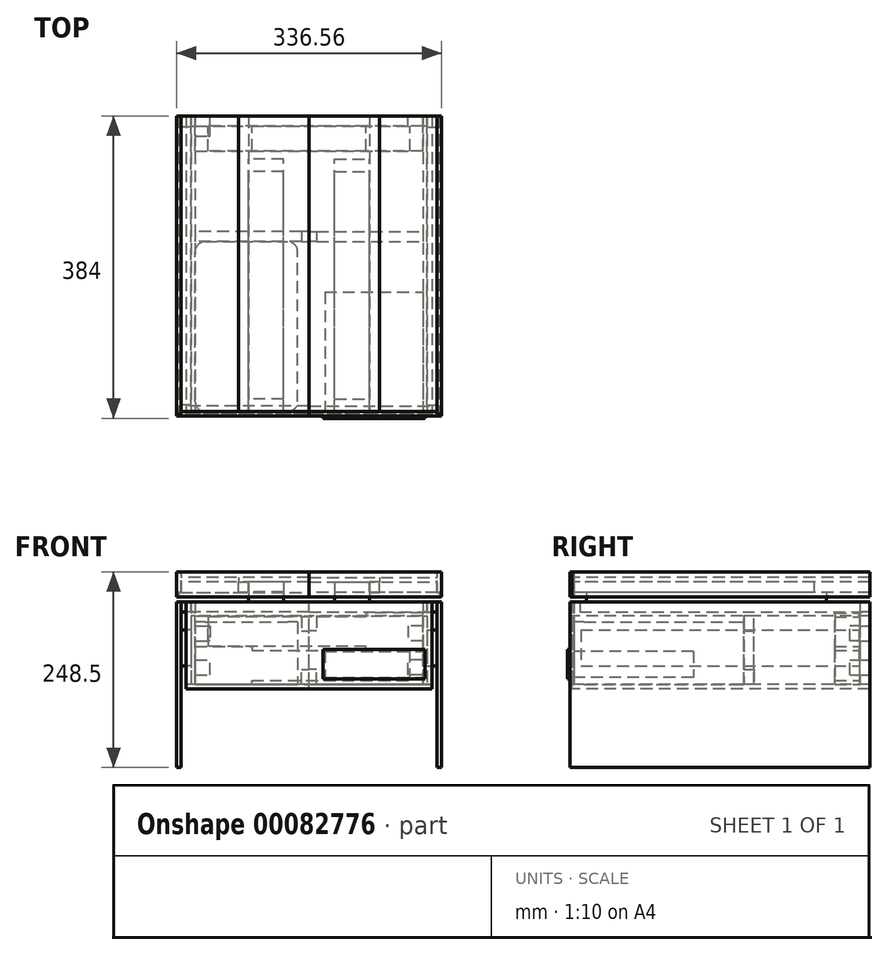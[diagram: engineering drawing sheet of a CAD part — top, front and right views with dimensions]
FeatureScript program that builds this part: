
annotation { "Feature Type Name" : "Feature", "Feature Type Description" : "" }
export const myFeature = defineFeature(function(context is Context, id is Id, definition is map)
    precondition{}
    {
        {
            var Q0;
            Q0=qCreatedBy(makeId("Front.planeOp"),FACE);
            var sketch = newSketch(context, id + "F0", { "sketchPlane" : qUnion([Q0])});
            skLineSegment(sketch, "E0.bottom", {"start": v(-168.28, 0) * mm, "end": v(-162.78, 0) * mm});
            skLineSegment(sketch, "E0.top", {"start": v(-168.28, 210.4) * mm, "end": v(-162.78, 210.4) * mm});
            skLineSegment(sketch, "E0.left", {"start": v(-168.28, 0) * mm, "end": v(-168.28, 210.4) * mm});
            skLineSegment(sketch, "E0.right", {"start": v(-162.78, 0) * mm, "end": v(-162.78, 210.4) * mm});
            skLineSegment(sketch, "E1", {"start": v(0, 0) * mm, "end": v(0, 336.55) * mm, "construction": true});
            skLineSegment(sketch, "E2", {"start": v(0, 235.8) * mm, "end": v(-127.03, 235.8) * mm, "construction": true});
            skLineSegment(sketch, "E3", {"start": v(-63.52, 235.8) * mm, "end": v(-63.52, 210.4) * mm, "construction": true});
            skLineSegment(sketch, "E4", {"start": v(-63.52, 210.4) * mm, "end": v(-12.72, 210.4) * mm, "construction": true});
            skLineSegment(sketch, "E5", {"start": v(-12.72, 210.4) * mm, "end": v(-12.72, 235.8) * mm, "construction": true});
            skLineSegment(sketch, "E6", {"start": v(0, 210.4) * mm, "end": v(-162.78, 210.4) * mm, "construction": true});
            skLineSegment(sketch, "E7", {"start": v(-162.78, 210.4) * mm, "end": v(-162.78, 197.7) * mm, "construction": true});
            skLineSegment(sketch, "E8", {"start": v(-162.78, 197.7) * mm, "end": v(0, 197.7) * mm, "construction": true});
            skLineSegment(sketch, "E9", {"start": v(-144.94, 222.25) * mm, "end": v(-144.94, 336.55) * mm, "construction": true});
            skLineSegment(sketch, "E10", {"start": v(-144.94, 336.55) * mm, "end": v(0, 336.55) * mm, "construction": true});
            skLineSegment(sketch, "E11", {"start": v(0, 0) * mm, "end": v(-82.93, 0) * mm, "construction": true});
            skLineSegment(sketch, "E12", {"start": v(-82.93, 0) * mm, "end": v(-82.93, 100) * mm, "construction": true});
            skLineSegment(sketch, "E13", {"start": v(0, 100) * mm, "end": v(-156.42, 100) * mm, "construction": true});
            skLineSegment(sketch, "E14", {"start": v(-156.42, 100) * mm, "end": v(-156.42, 105.5) * mm, "construction": true});
            skLineSegment(sketch, "E15", {"start": v(-156.42, 105.5) * mm, "end": v(0, 105.5) * mm, "construction": true});
            skLineSegment(sketch, "E16", {"start": v(0, 241.3) * mm, "end": v(-89.75, 241.3) * mm});
            skLineSegment(sketch, "E17", {"start": v(-89.75, 241.3) * mm, "end": v(-89.75, 235.8) * mm});
            skLineSegment(sketch, "E18", {"start": v(-89.75, 235.8) * mm, "end": v(0, 235.8) * mm});
            skLineSegment(sketch, "E19", {"start": v(0, 235.8) * mm, "end": v(0, 241.3) * mm});
            skLineSegment(sketch, "E20.bottom", {"start": v(-162.78, 222.25) * mm, "end": v(-77.05, 222.25) * mm});
            skLineSegment(sketch, "E20.top", {"start": v(-162.78, 216.75) * mm, "end": v(-77.05, 216.75) * mm});
            skLineSegment(sketch, "E20.left", {"start": v(-162.78, 222.25) * mm, "end": v(-162.78, 216.75) * mm, "construction": true});
            skLineSegment(sketch, "E20.right", {"start": v(-77.05, 222.25) * mm, "end": v(-77.05, 216.75) * mm});
            skLineSegment(sketch, "E21.bottom", {"start": v(-89.75, 235.8) * mm, "end": v(-77.05, 235.8) * mm});
            skLineSegment(sketch, "E21.top", {"start": v(-89.75, 222.25) * mm, "end": v(-77.05, 222.25) * mm, "construction": true});
            skLineSegment(sketch, "E21.left", {"start": v(-89.75, 235.8) * mm, "end": v(-89.75, 222.25) * mm, "construction": true});
            skLineSegment(sketch, "E21.right", {"start": v(-77.05, 235.8) * mm, "end": v(-77.05, 222.25) * mm, "construction": true});
            skLineSegment(sketch, "E22", {"start": v(-162.78, 310.09) * mm, "end": v(-162.78, 216.75) * mm, "construction": true});
            skLineSegment(sketch, "E23.bottom", {"start": v(-162.78, 128.74) * mm, "end": v(-150.08, 128.74) * mm, "construction": true});
            skLineSegment(sketch, "E23.top", {"start": v(-162.78, 174.46) * mm, "end": v(-150.08, 174.46) * mm, "construction": true});
            skLineSegment(sketch, "E23.left", {"start": v(-162.78, 128.74) * mm, "end": v(-162.78, 174.46) * mm, "construction": true});
            skLineSegment(sketch, "E23.right", {"start": v(-150.08, 128.74) * mm, "end": v(-150.08, 174.46) * mm, "construction": true});
            skPoint(sketch, "E24", {"position": v(-162.78, 151.6) * mm});
            skLineSegment(sketch, "E25", {"start": v(-162.78, 151.6) * mm, "end": v(-150.08, 151.6) * mm, "construction": true});
            skLineSegment(sketch, "E26", {"start": v(-150.08, 197.7) * mm, "end": v(-150.08, 105.5) * mm, "construction": true});
            skLineSegment(sketch, "E27", {"start": v(-156.42, 100) * mm, "end": v(-156.43, 210.4) * mm, "construction": true});
            skLineSegment(sketch, "E28", {"start": v(-156.43, 210.4) * mm, "end": v(0, 210.4) * mm, "construction": true});
            skLineSegment(sketch, "E29", {"start": v(0, 210.4) * mm, "end": v(0, 100) * mm, "construction": true});
            skLineSegment(sketch, "E30", {"start": v(-77.05, 216.75) * mm, "end": v(-77.05, 210.4) * mm, "construction": true});
            skLineSegment(sketch, "E31", {"start": v(-156.43, 181.35) * mm, "end": v(-162.78, 181.35) * mm, "construction": true});
            skLineSegment(sketch, "E32.bottom", {"start": v(-144.58, 105.5) * mm, "end": v(-150.08, 105.5) * mm, "construction": true});
            skLineSegment(sketch, "E32.top", {"start": v(-144.58, 192.2) * mm, "end": v(-150.08, 192.2) * mm, "construction": true});
            skLineSegment(sketch, "E32.left", {"start": v(-144.58, 105.5) * mm, "end": v(-144.58, 192.2) * mm, "construction": true});
            skLineSegment(sketch, "E32.right", {"start": v(-150.08, 105.5) * mm, "end": v(-150.08, 192.2) * mm, "construction": true});
            skLineSegment(sketch, "E33", {"start": v(-144.58, 192.2) * mm, "end": v(-144.58, 197.7) * mm, "construction": true});
            skLineSegment(sketch, "E34", {"start": v(-162.78, 222.25) * mm, "end": v(-165.52, 222.25) * mm});
            skLineSegment(sketch, "E35", {"start": v(-165.52, 216.75) * mm, "end": v(-162.78, 216.75) * mm});
            skLineSegment(sketch, "E36", {"start": v(-162.78, 216.75) * mm, "end": v(-165.52, 216.75) * mm});
            skLineSegment(sketch, "E37", {"start": v(-165.52, 222.25) * mm, "end": v(-165.52, 216.75) * mm});
            skLineSegment(sketch, "E38", {"start": v(-165.52, 216.75) * mm, "end": v(-165.52, 210.4) * mm, "construction": true});
            skLineSegment(sketch, "E39", {"start": v(-165.53, 210.4) * mm, "end": v(-170.23, 215.23) * mm, "construction": true});
            skSolve(sketch);
        }
        {
            var Q0;
            Q0=makeQuery(id+"F0.imprint","IMPRINT",FACE,{"disambiguationData":[TD([[makeQuery(id+"F0.imprint","IMPRINT",EDGE,{"derivedFrom":sQuery(id+"F0.wireOp",EDGE,"E0.bottom")}),1.0]])]});
            var Q1;
            Q1=makeQuery(id+"F0.imprint","IMPRINT",FACE,{"disambiguationData":[TD([[makeQuery(id+"F0.imprint","IMPRINT",EDGE,{"derivedFrom":sQuery(id+"F0.wireOp",EDGE,"E20.bottom")}),-1.0]])]});
            var Q2;
            Q2=makeQuery(id+"F0.imprint","IMPRINT",FACE,{"disambiguationData":[TD([[makeQuery(id+"F0.imprint","IMPRINT",EDGE,{"derivedFrom":sQuery(id+"F0.wireOp",EDGE,"E16")}),1.0]])]});
            var Q3;
            Q3 = qConstructionFilter(qBodyType(qCreatedBy(id + "F0" ,EDGE), BodyType.WIRE), ConstructionObject.NO);
            extrude(context, id + "F1", {"entities" : qUnion([Q0, Q1, Q2]), "surfaceEntities" : qUnion([Q3]), "oppositeDirection" : true, "depth" : 381 * mm});
        }
        {
            var Q0;
            Q0=qCreatedBy(makeId("Front.planeOp"),FACE);
            var sketch = newSketch(context, id + "F2", { "sketchPlane" : qUnion([Q0])});
            skLineSegment(sketch, "E40.bottom", {"start": v(0, 100) * mm, "end": v(-156.43, 100) * mm});
            skLineSegment(sketch, "E40.top", {"start": v(0, 210.4) * mm, "end": v(-156.43, 210.4) * mm});
            skLineSegment(sketch, "E40.left", {"start": v(0, 100) * mm, "end": v(0, 210.4) * mm});
            skLineSegment(sketch, "E40.right", {"start": v(-156.43, 100) * mm, "end": v(-156.43, 210.4) * mm});
            skSolve(sketch);
        }
        {
            var Q0;
            Q0=makeQuery(id+"F2.imprint","IMPRINT",FACE,{"disambiguationData":[TD([[makeQuery(id+"F2.imprint","IMPRINT",EDGE,{"derivedFrom":sQuery(id+"F2.wireOp",EDGE,"E40.bottom")}),-1.0]])]});
            extrude(context, id + "F3", {"entities" : qUnion([Q0]), "oppositeDirection" : true, "depth" : 5.5 * mm});
        }
        {
            var Q0;
            Q0=makeQuery(id+"F1.opExtrude","SWEPT_FACE",FACE,{"disambiguationData":[OSD([sQuery(id+"F0.wireOp",EDGE,"E0.right")])]});
            var sketch = newSketch(context, id + "F4", { "sketchPlane" : qUnion([Q0])});
            skLineSegment(sketch, "E41.bottom", {"start": v(13.97, 174.46) * mm, "end": v(367.03, 174.46) * mm});
            skLineSegment(sketch, "E41.top", {"start": v(13.97, 128.74) * mm, "end": v(367.03, 128.74) * mm});
            skLineSegment(sketch, "E41.left", {"start": v(13.97, 174.46) * mm, "end": v(13.97, 128.74) * mm});
            skLineSegment(sketch, "E41.right", {"start": v(367.03, 174.46) * mm, "end": v(367.03, 128.74) * mm});
            skLineSegment(sketch, "E42", {"start": v(13.97, 174.46) * mm, "end": v(0, 174.46) * mm, "construction": true});
            skLineSegment(sketch, "E43", {"start": v(13.97, 128.74) * mm, "end": v(0, 128.74) * mm, "construction": true});
            skLineSegment(sketch, "E44", {"start": v(190.5, 128.74) * mm, "end": v(190.5, 210.4) * mm, "construction": true});
            skSolve(sketch);
        }
        {
            var Q0;
            Q0=makeQuery(id+"F4.imprint","IMPRINT",FACE,{"disambiguationData":[TD([[makeQuery(id+"F4.imprint","IMPRINT",EDGE,{"derivedFrom":sQuery(id+"F4.wireOp",EDGE,"E41.bottom")}),-1.0]])]});
            extrude(context, id + "F5", {"entities" : qUnion([Q0]), "depth" : 12.7 * mm});
        }
        {
            var Q0;
            Q0=makeQuery(id+"F3.opExtrude","CAP_FACE",FACE,{"disambiguationData":[OSD([sQuery(id+"F2.wireOp",EDGE,"E40.bottom"),sQuery(id+"F2.wireOp",EDGE,"E40.top"),sQuery(id+"F2.wireOp",EDGE,"E40.left"),sQuery(id+"F2.wireOp",EDGE,"E40.right")])],"isStart":false});
            var sketch = newSketch(context, id + "F6", { "sketchPlane" : qUnion([Q0])});
            skLineSegment(sketch, "E45.bottom", {"start": v(0, 100) * mm, "end": v(156.42, 100) * mm});
            skLineSegment(sketch, "E45.top", {"start": v(0, 105.5) * mm, "end": v(144.58, 105.5) * mm});
            skLineSegment(sketch, "E45.left", {"start": v(0, 100) * mm, "end": v(0, 105.5) * mm});
            skLineSegment(sketch, "E45.right", {"start": v(156.42, 100) * mm, "end": v(156.42, 105.5) * mm});
            skLineSegment(sketch, "E46.bottom", {"start": v(144.58, 210.4) * mm, "end": v(150.08, 210.4) * mm});
            skLineSegment(sketch, "E46.left", {"start": v(144.58, 210.4) * mm, "end": v(144.58, 105.5) * mm});
            skLineSegment(sketch, "E46.right", {"start": v(150.08, 210.4) * mm, "end": v(150.08, 105.5) * mm});
            skLineSegment(sketch, "E47.trimOffspring", {"start": v(150.08, 105.5) * mm, "end": v(156.42, 105.5) * mm});
            skSolve(sketch);
        }
        {
            var Q0;
            Q0 = qSketchRegion(id + "F6", true);
            extrude(context, id + "F7", {"entities" : qUnion([Q0]), "operationType" : NewBodyOperationType.REMOVE, "oppositeDirection" : true, "depth" : 5.5 * mm / 2});
        }
        {
            var Q0;
            Q0=makeQuery(id+"F0.imprint","IMPRINT",FACE,{"disambiguationData":[TD([[makeQuery(id+"F0.imprint","IMPRINT",EDGE,{"derivedFrom":sQuery(id+"F0.wireOp",EDGE,"E16")}),1.0]])]});
            var Q1;
            Q1=makeQuery(id+"F0.imprint","IMPRINT",FACE,{"disambiguationData":[TD([[makeQuery(id+"F0.imprint","IMPRINT",EDGE,{"derivedFrom":sQuery(id+"F0.wireOp",EDGE,"E20.bottom")}),-1.0]])]});
            extrude(context, id + "F8", {"entities" : qUnion([Q0, Q1]), "operationType" : NewBodyOperationType.REMOVE, "oppositeDirection" : true, "depth" : 5.5 * mm / 2});
        }
        {
            var Q0;
            Q0=makeQuery(id+"F3.opExtrude","CAP_FACE",FACE,{"disambiguationData":[OSD([sQuery(id+"F2.wireOp",EDGE,"E40.bottom"),sQuery(id+"F2.wireOp",EDGE,"E40.top"),sQuery(id+"F2.wireOp",EDGE,"E40.left"),sQuery(id+"F2.wireOp",EDGE,"E40.right")])],"isStart":true});
            var sketch = newSketch(context, id + "F9", { "sketchPlane" : qUnion([Q0])});
            skLineSegment(sketch, "E48.bottom", {"start": v(0, 248.5) * mm, "end": v(-168.28, 248.5) * mm});
            skLineSegment(sketch, "E48.top", {"start": v(0, 216.75) * mm, "end": v(-168.28, 216.75) * mm});
            skLineSegment(sketch, "E48.left", {"start": v(0, 248.5) * mm, "end": v(0, 216.75) * mm});
            skLineSegment(sketch, "E48.right", {"start": v(-168.28, 248.5) * mm, "end": v(-168.28, 216.75) * mm});
            skLineSegment(sketch, "E49", {"start": v(-168.28, 216.75) * mm, "end": v(-168.28, 188.12) * mm, "construction": true});
            skSolve(sketch);
        }
        {
            var Q0;
            Q0=makeQuery(id+"F9.imprint","IMPRINT",FACE,{"disambiguationData":[TD([[makeQuery(id+"F9.imprint","IMPRINT",EDGE,{"derivedFrom":sQuery(id+"F9.wireOp",EDGE,"E48.bottom")}),1.0]])]});
            extrude(context, id + "F10", {"entities" : qUnion([Q0]), "oppositeDirection" : true, "depth" : 5.5 * mm});
        }
        {
            var Q0;
            Q0=makeQuery(id+"F10.opExtrude","CAP_FACE",FACE,{"disambiguationData":[OSD([sQuery(id+"F9.wireOp",EDGE,"E48.bottom"),sQuery(id+"F9.wireOp",EDGE,"E48.top"),sQuery(id+"F9.wireOp",EDGE,"E48.left"),sQuery(id+"F9.wireOp",EDGE,"E48.right")])],"isStart":false});
            var sketch = newSketch(context, id + "F11", { "sketchPlane" : qUnion([Q0])});
            skLineSegment(sketch, "E50.bottom", {"start": v(0, 241.3) * mm, "end": v(162.78, 241.3) * mm});
            skLineSegment(sketch, "E50.top", {"start": v(0, 235.8) * mm, "end": v(162.78, 235.8) * mm});
            skLineSegment(sketch, "E50.left", {"start": v(0, 241.3) * mm, "end": v(0, 235.8) * mm});
            skLineSegment(sketch, "E51.bottom", {"start": v(168.28, 248.5) * mm, "end": v(162.78, 248.5) * mm});
            skLineSegment(sketch, "E51.top", {"start": v(168.28, 216.75) * mm, "end": v(162.78, 216.75) * mm});
            skLineSegment(sketch, "E51.left", {"start": v(168.28, 248.5) * mm, "end": v(168.28, 216.75) * mm});
            skLineSegment(sketch, "E51.right", {"start": v(162.78, 248.5) * mm, "end": v(162.78, 241.3) * mm});
            skLineSegment(sketch, "E52.bottom", {"start": v(162.78, 222.25) * mm, "end": v(0, 222.25) * mm});
            skLineSegment(sketch, "E52.top", {"start": v(162.78, 216.75) * mm, "end": v(0, 216.75) * mm});
            skLineSegment(sketch, "E52.right", {"start": v(0, 222.25) * mm, "end": v(0, 216.75) * mm});
            skLineSegment(sketch, "E53.trimOffspring", {"start": v(162.78, 235.8) * mm, "end": v(162.78, 222.25) * mm});
            skSolve(sketch);
        }
        {
            var Q0;
            Q0 = qSketchRegion(id + "F11", true);
            extrude(context, id + "F12", {"entities" : qUnion([Q0]), "operationType" : NewBodyOperationType.REMOVE, "oppositeDirection" : true, "depth" : 5.5 * mm / 2});
        }
        {
            var Q0;
            Q0=makeQuery(id+"F1.opExtrude","SWEPT_FACE",FACE,{"disambiguationData":[OSD([sQuery(id+"F0.wireOp",EDGE,"E0.right")])]});
            var sketch = newSketch(context, id + "F13", { "sketchPlane" : qUnion([Q0])});
            skLineSegment(sketch, "E54.bottom", {"start": v(12.7, 210.4) * mm, "end": v(381, 210.4) * mm});
            skLineSegment(sketch, "E54.top", {"start": v(12.7, 197.7) * mm, "end": v(381, 197.7) * mm});
            skLineSegment(sketch, "E54.left", {"start": v(12.7, 210.4) * mm, "end": v(12.7, 197.7) * mm});
            skLineSegment(sketch, "E54.right", {"start": v(381, 210.4) * mm, "end": v(381, 197.7) * mm});
            skSolve(sketch);
        }
        {
            var Q0;
            Q0=makeQuery(id+"F13.imprint","IMPRINT",FACE,{"disambiguationData":[TD([[makeQuery(id+"F13.imprint","IMPRINT",EDGE,{"derivedFrom":sQuery(id+"F13.wireOp",EDGE,"E54.bottom")}),1.0]])]});
            var Q1;
            Q1=makeQuery(id+"F3.opExtrude","SWEPT_FACE",FACE,{"disambiguationData":[OSD([sQuery(id+"F2.wireOp",EDGE,"E40.left")])]});
            extrude(context, id + "F14", {"entities" : qUnion([Q0]), "endBound" : BoundingType.UP_TO_SURFACE, "endBoundEntityFace" : qUnion([Q1]), "depth" : 25.4 * mm});
        }
        {
            var Q0;
            {var subQ0=sQuery(id+"F9.wireOp",EDGE,"E48.left");Q0=makeQuery(id+"F12.boolean.opBoolean","SPLIT",FACE,{"disambiguationData":[TD([makeQuery(id+"F12.opExtrude","SWEPT_FACE",FACE,{"disambiguationData":[OSD([sQuery(id+"F11.wireOp",EDGE,"E50.top")])]})])],"derivedFrom":makeQuery(id+"F10.opExtrude","CAP_FACE",FACE,{"disambiguationData":[OSD([sQuery(id+"F9.wireOp",EDGE,"E48.bottom"),sQuery(id+"F9.wireOp",EDGE,"E48.top"),subQ0,sQuery(id+"F9.wireOp",EDGE,"E48.right")])],"isStart":false})});}
            var sketch = newSketch(context, id + "F15", { "sketchPlane" : qUnion([Q0])});
            skLineSegment(sketch, "E55.bottom", {"start": v(89.75, 235.8) * mm, "end": v(77.05, 235.8) * mm});
            skLineSegment(sketch, "E55.top", {"start": v(89.75, 222.25) * mm, "end": v(77.05, 222.25) * mm});
            skLineSegment(sketch, "E55.left", {"start": v(89.75, 235.8) * mm, "end": v(89.75, 222.25) * mm});
            skLineSegment(sketch, "E55.right", {"start": v(77.05, 235.8) * mm, "end": v(77.05, 222.25) * mm});
            skSolve(sketch);
        }
        {
            var Q0;
            Q0=makeQuery(id+"F15.imprint","IMPRINT",FACE,{"disambiguationData":[TD([[makeQuery(id+"F15.imprint","IMPRINT",EDGE,{"derivedFrom":sQuery(id+"F15.wireOp",EDGE,"E55.bottom")}),-1.0]])]});
            var Q1;
            Q1=makeQuery(id+"F1.opExtrude","CAP_FACE",FACE,{"disambiguationData":[OSD([sQuery(id+"F0.wireOp",EDGE,"E16"),sQuery(id+"F0.wireOp",EDGE,"E17"),sQuery(id+"F0.wireOp",EDGE,"E18"),sQuery(id+"F0.wireOp",EDGE,"E19"),sQuery(id+"F0.wireOp",EDGE,"E21.bottom")])],"isStart":false});
            extrude(context, id + "F16", {"entities" : qUnion([Q0]), "endBound" : BoundingType.UP_TO_SURFACE, "endBoundEntityFace" : qUnion([Q1]), "depth" : 25.4 * mm});
        }
        {
            var Q0;
            Q0=makeQuery(id+"F12.boolean.opBoolean","COPY",FACE,{"derivedFrom":makeQuery(id+"F12.opExtrude","CAP_FACE",FACE,{"disambiguationData":[OSD([sQuery(id+"F11.wireOp",EDGE,"E50.bottom"),sQuery(id+"F11.wireOp",EDGE,"E50.top"),sQuery(id+"F11.wireOp",EDGE,"E50.left"),sQuery(id+"F11.wireOp",EDGE,"E51.bottom"),sQuery(id+"F11.wireOp",EDGE,"E51.top"),sQuery(id+"F11.wireOp",EDGE,"E51.left"),sQuery(id+"F11.wireOp",EDGE,"E51.right"),sQuery(id+"F11.wireOp",EDGE,"E52.bottom"),sQuery(id+"F11.wireOp",EDGE,"E52.top"),sQuery(id+"F11.wireOp",EDGE,"E52.right"),sQuery(id+"F11.wireOp",EDGE,"E53.trimOffspring")])],"isStart":false})});
            var sketch = newSketch(context, id + "F17", { "sketchPlane" : qUnion([Q0])});
            skLineSegment(sketch, "E56.bottom", {"start": v(168.28, 248.5) * mm, "end": v(162.78, 248.5) * mm});
            skLineSegment(sketch, "E56.top", {"start": v(168.28, 216.75) * mm, "end": v(165.53, 216.75) * mm});
            skLineSegment(sketch, "E56.left", {"start": v(168.28, 248.5) * mm, "end": v(168.28, 216.75) * mm});
            skLineSegment(sketch, "E56.right", {"start": v(162.78, 248.5) * mm, "end": v(162.78, 222.25) * mm});
            skLineSegment(sketch, "E57.top", {"start": v(165.53, 222.25) * mm, "end": v(162.78, 222.25) * mm});
            skLineSegment(sketch, "E57.left", {"start": v(165.53, 216.75) * mm, "end": v(165.53, 222.25) * mm});
            skPoint(sketch, "E58.orphan", {"position": v(162.78, 216.75) * mm});
            skSolve(sketch);
        }
        {
            var Q0;
            {var subQ2=sQuery(id+"F17.wireOp",EDGE,"E56.bottom");Q0=makeQuery(id+"F17.imprint","IMPRINT",FACE,{"disambiguationData":[TD([[makeQuery(id+"F17.imprint","IMPRINT",EDGE,{"derivedFrom":subQ2}),-1.0]])]});}
            var Q1;
            Q1=makeQuery(id+"F1.opExtrude","CAP_FACE",FACE,{"disambiguationData":[OSD([sQuery(id+"F0.wireOp",EDGE,"E20.bottom"),sQuery(id+"F0.wireOp",EDGE,"E20.top"),sQuery(id+"F0.wireOp",EDGE,"E20.left"),sQuery(id+"F0.wireOp",EDGE,"E20.right")])],"isStart":false});
            extrude(context, id + "F18", {"entities" : qUnion([Q0]), "endBound" : BoundingType.UP_TO_SURFACE, "endBoundEntityFace" : qUnion([Q1]), "depth" : 25.4 * mm});
        }
        {
            var Q0;
            Q0=makeQuery(id+"F14.opExtrude","SWEPT_FACE",FACE,{"disambiguationData":[OSD([sQuery(id+"F13.wireOp",EDGE,"E54.right")])]});
            var sketch = newSketch(context, id + "F19", { "sketchPlane" : qUnion([Q0])});
            skLineSegment(sketch, "E59.bottom", {"start": v(150.08, 105.5) * mm, "end": v(0, 105.5) * mm});
            skLineSegment(sketch, "E59.top", {"start": v(150.08, 192.2) * mm, "end": v(0, 192.2) * mm});
            skLineSegment(sketch, "E59.left", {"start": v(150.08, 105.5) * mm, "end": v(150.08, 192.2) * mm});
            skLineSegment(sketch, "E59.right", {"start": v(0, 105.5) * mm, "end": v(0, 192.2) * mm});
            skSolve(sketch);
        }
        {
            var Q0;
            Q0=makeQuery(id+"F19.imprint","IMPRINT",FACE,{"disambiguationData":[TD([[makeQuery(id+"F19.imprint","IMPRINT",EDGE,{"derivedFrom":sQuery(id+"F19.wireOp",EDGE,"E59.bottom")}),-1.0]])]});
            extrude(context, id + "F20", {"entities" : qUnion([Q0]), "oppositeDirection" : true, "depth" : 12.7 * mm});
        }
        {
            var Q0;
            Q0=makeQuery(id+"F20.opExtrude","CAP_FACE",FACE,{"disambiguationData":[OSD([sQuery(id+"F19.wireOp",EDGE,"E59.bottom"),sQuery(id+"F19.wireOp",EDGE,"E59.top"),sQuery(id+"F19.wireOp",EDGE,"E59.left"),sQuery(id+"F19.wireOp",EDGE,"E59.right")])],"isStart":false});
            var sketch = newSketch(context, id + "F21", { "sketchPlane" : qUnion([Q0])});
            skLineSegment(sketch, "E60.0.0", {"start": v(-144.58, 105.5) * mm, "end": v(0, 105.5) * mm});
            skLineSegment(sketch, "E60.0.1", {"start": v(0, 105.5) * mm, "end": v(0, 100) * mm});
            skLineSegment(sketch, "E60.0.2", {"start": v(0, 100) * mm, "end": v(-156.43, 100) * mm});
            skLineSegment(sketch, "E60.0.3", {"start": v(-156.43, 100) * mm, "end": v(-156.43, 105.5) * mm});
            skLineSegment(sketch, "E60.0.4", {"start": v(-156.43, 105.5) * mm, "end": v(-150.08, 105.5) * mm});
            skLineSegment(sketch, "E60.0.5", {"start": v(-150.08, 105.5) * mm, "end": v(-150.08, 210.4) * mm});
            skLineSegment(sketch, "E60.0.6", {"start": v(-150.08, 210.4) * mm, "end": v(-144.58, 210.4) * mm});
            skLineSegment(sketch, "E60.0.7", {"start": v(-144.58, 210.4) * mm, "end": v(-144.58, 105.5) * mm});
            skSolve(sketch);
        }
        {
            var Q0;
            Q0 = qSketchRegion(id + "F21", true);
            extrude(context, id + "F22", {"entities" : qUnion([Q0]), "operationType" : NewBodyOperationType.REMOVE, "oppositeDirection" : true, "depth" : 25.4 * mm});
        }
        {
            var Q0;
            Q0=makeQuery(id+"F7.boolean.opBoolean","COPY",FACE,{"derivedFrom":makeQuery(id+"F7.opExtrude","CAP_FACE",FACE,{"disambiguationData":[OSD([sQuery(id+"F6.wireOp",EDGE,"E45.bottom"),sQuery(id+"F6.wireOp",EDGE,"E45.top"),sQuery(id+"F6.wireOp",EDGE,"E45.left"),sQuery(id+"F6.wireOp",EDGE,"E45.right"),sQuery(id+"F6.wireOp",EDGE,"E46.bottom"),sQuery(id+"F6.wireOp",EDGE,"E46.left"),sQuery(id+"F6.wireOp",EDGE,"E46.right"),sQuery(id+"F6.wireOp",EDGE,"E47.trimOffspring")])],"isStart":false})});
            var sketch = newSketch(context, id + "F23", { "sketchPlane" : qUnion([Q0])});
            skLineSegment(sketch, "E61.bottom", {"start": v(0, 100) * mm, "end": v(156.43, 100) * mm});
            skLineSegment(sketch, "E61.top", {"start": v(0, 105.5) * mm, "end": v(156.43, 105.5) * mm});
            skLineSegment(sketch, "E61.left", {"start": v(0, 100) * mm, "end": v(0, 105.5) * mm});
            skLineSegment(sketch, "E61.right", {"start": v(156.43, 100) * mm, "end": v(156.43, 105.5) * mm});
            skSolve(sketch);
        }
        {
            var Q0;
            Q0=makeQuery(id+"F23.imprint","IMPRINT",FACE,{"disambiguationData":[TD([[makeQuery(id+"F23.imprint","IMPRINT",EDGE,{"derivedFrom":sQuery(id+"F23.wireOp",EDGE,"E61.bottom")}),1.0]])]});
            var Q1;
            Q1=makeQuery(id+"F20.opExtrude","CAP_FACE",FACE,{"disambiguationData":[OSD([sQuery(id+"F19.wireOp",EDGE,"E59.bottom"),sQuery(id+"F19.wireOp",EDGE,"E59.top"),sQuery(id+"F19.wireOp",EDGE,"E59.left"),sQuery(id+"F19.wireOp",EDGE,"E59.right")])],"isStart":true});
            extrude(context, id + "F24", {"entities" : qUnion([Q0]), "endBound" : BoundingType.UP_TO_SURFACE, "endBoundEntityFace" : qUnion([Q1]), "depth" : 367 * mm});
        }
        {
            var Q0;
            Q0=makeQuery(id+"F7.boolean.opBoolean","COPY",FACE,{"derivedFrom":makeQuery(id+"F7.opExtrude","CAP_FACE",FACE,{"disambiguationData":[OSD([sQuery(id+"F6.wireOp",EDGE,"E45.bottom"),sQuery(id+"F6.wireOp",EDGE,"E45.top"),sQuery(id+"F6.wireOp",EDGE,"E45.left"),sQuery(id+"F6.wireOp",EDGE,"E45.right"),sQuery(id+"F6.wireOp",EDGE,"E46.bottom"),sQuery(id+"F6.wireOp",EDGE,"E46.left"),sQuery(id+"F6.wireOp",EDGE,"E46.right"),sQuery(id+"F6.wireOp",EDGE,"E47.trimOffspring")])],"isStart":false})});
            var sketch = newSketch(context, id + "F25", { "sketchPlane" : qUnion([Q0])});
            skLineSegment(sketch, "E62.bottom", {"start": v(144.58, 192.2) * mm, "end": v(150.08, 192.2) * mm});
            skLineSegment(sketch, "E62.top", {"start": v(144.58, 105.5) * mm, "end": v(150.08, 105.5) * mm});
            skLineSegment(sketch, "E62.left", {"start": v(144.58, 192.2) * mm, "end": v(144.58, 105.5) * mm});
            skLineSegment(sketch, "E62.right", {"start": v(150.08, 192.2) * mm, "end": v(150.08, 105.5) * mm});
            skSolve(sketch);
        }
        {
            var Q0;
            Q0=makeQuery(id+"F25.imprint","IMPRINT",FACE,{"disambiguationData":[TD([[makeQuery(id+"F25.imprint","IMPRINT",EDGE,{"derivedFrom":sQuery(id+"F25.wireOp",EDGE,"E62.bottom")}),-1.0]])]});
            var Q1;
            Q1=makeQuery(id+"F24.opExtrude","CAP_FACE",FACE,{"disambiguationData":[OSD([sQuery(id+"F23.wireOp",EDGE,"E61.bottom"),sQuery(id+"F23.wireOp",EDGE,"E61.top"),sQuery(id+"F23.wireOp",EDGE,"E61.left"),sQuery(id+"F23.wireOp",EDGE,"E61.right")])],"isStart":false});
            extrude(context, id + "F26", {"entities" : qUnion([Q0]), "endBound" : BoundingType.UP_TO_SURFACE, "endBoundEntityFace" : qUnion([Q1]), "depth" : 25.4 * mm});
        }
        {
            var Q0;
            Q0=makeQuery(id+"F24.opExtrude","SWEPT_FACE",FACE,{"disambiguationData":[OSD([sQuery(id+"F23.wireOp",EDGE,"E61.top")])]});
            var sketch = newSketch(context, id + "F27", { "sketchPlane" : qUnion([Q0])});
            skLineSegment(sketch, "E63.bottom", {"start": v(-131.88, 5.5) * mm, "end": v(-27.1, 5.5) * mm});
            skLineSegment(sketch, "E63.top", {"start": v(-131.88, 221.4) * mm, "end": v(-27.1, 221.4) * mm});
            skLineSegment(sketch, "E63.left", {"start": v(-144.58, 18.2) * mm, "end": v(-144.58, 208.7) * mm});
            skLineSegment(sketch, "E63.right", {"start": v(-14.4, 18.2) * mm, "end": v(-14.4, 208.7) * mm});
            skPoint(sketch, "E64.visualSharp", {"position": v(-14.4, 5.5) * mm});
            skArc(sketch, "E64.filletArc", {"start": v(-27.1, 5.5) * mm, "mid": v(-18.12, 9.22) * mm, "end": v(-14.4, 18.2) * mm});
            skPoint(sketch, "E65.visualSharp", {"position": v(-14.4, 221.4) * mm});
            skArc(sketch, "E65.filletArc", {"start": v(-14.4, 208.7) * mm, "mid": v(-18.12, 217.68) * mm, "end": v(-27.1, 221.4) * mm});
            skPoint(sketch, "E66.visualSharp", {"position": v(-144.58, 221.4) * mm});
            skArc(sketch, "E66.filletArc", {"start": v(-131.88, 221.4) * mm, "mid": v(-140.86, 217.68) * mm, "end": v(-144.58, 208.7) * mm});
            skPoint(sketch, "E67.visualSharp", {"position": v(-144.58, 5.5) * mm});
            skArc(sketch, "E67.filletArc", {"start": v(-144.58, 18.2) * mm, "mid": v(-140.86, 9.22) * mm, "end": v(-131.88, 5.5) * mm});
            skSolve(sketch);
        }
        {
            var Q0;
            Q0=makeQuery(id+"F27.imprint","IMPRINT",FACE,{"disambiguationData":[TD([[makeQuery(id+"F27.imprint","IMPRINT",EDGE,{"derivedFrom":sQuery(id+"F27.wireOp",EDGE,"E63.bottom")}),1.0]])]});
            extrude(context, id + "F28", {"entities" : qUnion([Q0]), "depth" : 79.38 * mm});
        }
        {
            var Q0;
            Q0=makeQuery(id+"F28.opExtrude","SWEPT_FACE",FACE,{"disambiguationData":[OSD([sQuery(id+"F27.wireOp",EDGE,"E63.top")])]});
            var sketch = newSketch(context, id + "F29", { "sketchPlane" : qUnion([Q0])});
            skLineSegment(sketch, "E68.bottom", {"start": v(0, 105.5) * mm, "end": v(144.58, 105.5) * mm});
            skLineSegment(sketch, "E68.top", {"start": v(0, 192.2) * mm, "end": v(144.58, 192.2) * mm});
            skLineSegment(sketch, "E68.left", {"start": v(0, 105.5) * mm, "end": v(0, 192.2) * mm});
            skLineSegment(sketch, "E68.right", {"start": v(144.58, 105.5) * mm, "end": v(144.58, 192.2) * mm});
            skSolve(sketch);
        }
        {
            var Q0;
            Q0 = qSketchRegion(id + "F29", true);
            extrude(context, id + "F30", {"entities" : qUnion([Q0]), "depth" : 12.7 * mm});
        }
        {
            var Q0;
            Q0=makeQuery(id+"F30.opExtrude","CAP_FACE",FACE,{"disambiguationData":[OSD([sQuery(id+"F29.wireOp",EDGE,"E68.bottom"),sQuery(id+"F29.wireOp",EDGE,"E68.top"),sQuery(id+"F29.wireOp",EDGE,"E68.left"),sQuery(id+"F29.wireOp",EDGE,"E68.right")])],"isStart":true});
            var sketch = newSketch(context, id + "F31", { "sketchPlane" : qUnion([Q0])});
            skLineSegment(sketch, "E69.bottom", {"start": v(-9.52, 192.2) * mm, "end": v(9.53, 192.2) * mm});
            skLineSegment(sketch, "E69.top", {"start": v(-9.52, 173.15) * mm, "end": v(9.53, 173.15) * mm});
            skLineSegment(sketch, "E69.left", {"start": v(-9.52, 192.2) * mm, "end": v(-9.52, 173.15) * mm});
            skLineSegment(sketch, "E69.right", {"start": v(9.53, 192.2) * mm, "end": v(9.53, 173.15) * mm});
            skPoint(sketch, "E69.middle", {"position": v(0, 182.68) * mm});
            skLineSegment(sketch, "E70", {"start": v(0, 192.2) * mm, "end": v(0, 105.5) * mm, "construction": true});
            skLineSegment(sketch, "E71", {"start": v(0, 148.85) * mm, "end": v(28.16, 148.85) * mm, "construction": true});
            skLineSegment(sketch, "E72.MirrorCS", {"start": v(-9.52, 105.5) * mm, "end": v(9.53, 105.5) * mm});
            skLineSegment(sketch, "E73.MirrorCS", {"start": v(-9.52, 124.55) * mm, "end": v(9.53, 124.55) * mm});
            skPoint(sketch, "E74.MirrorP", {"position": v(0, 115.02) * mm});
            skLineSegment(sketch, "E75.MirrorCS", {"start": v(9.53, 105.5) * mm, "end": v(9.53, 124.55) * mm});
            skLineSegment(sketch, "E76.MirrorCS", {"start": v(-9.52, 105.5) * mm, "end": v(-9.52, 124.55) * mm});
            skSolve(sketch);
        }
        {
            var Q0;
            Q0 = qSketchRegion(id + "F31", true);
            extrude(context, id + "F32", {"entities" : qUnion([Q0]), "operationType" : NewBodyOperationType.REMOVE, "oppositeDirection" : true, "depth" : 25.4 * mm});
        }
        {
            var Q0;
            Q0=makeQuery(id+"F20.opExtrude","CAP_FACE",FACE,{"disambiguationData":[OSD([sQuery(id+"F19.wireOp",EDGE,"E59.bottom"),sQuery(id+"F19.wireOp",EDGE,"E59.top"),sQuery(id+"F19.wireOp",EDGE,"E59.left"),sQuery(id+"F19.wireOp",EDGE,"E59.right")])],"isStart":false});
            var sketch = newSketch(context, id + "F33", { "sketchPlane" : qUnion([Q0])});
            skPoint(sketch, "E77.oppositeSnap0", {"position": v(-144.58, 148.85) * mm});
            skLineSegment(sketch, "E78", {"start": v(-144.58, 105.5) * mm, "end": v(-144.58, 153.5) * mm});
            skLineSegment(sketch, "E79", {"start": v(-144.58, 153.5) * mm, "end": v(-72.58, 153.5) * mm});
            skLineSegment(sketch, "E80", {"start": v(-72.58, 153.5) * mm, "end": v(-72.58, 148.5) * mm});
            skLineSegment(sketch, "E81", {"start": v(-72.58, 148.5) * mm, "end": v(128.47, 148.5) * mm});
            skLineSegment(sketch, "E82", {"start": v(128.47, 148.5) * mm, "end": v(128.47, 129.5) * mm});
            skLineSegment(sketch, "E83", {"start": v(128.47, 129.5) * mm, "end": v(-144.58, 129.5) * mm, "construction": true});
            skLineSegment(sketch, "E84.MirrorCS", {"start": v(128.47, 110.5) * mm, "end": v(128.47, 129.5) * mm});
            skLineSegment(sketch, "E85.MirrorCS", {"start": v(-72.58, 110.5) * mm, "end": v(128.47, 110.5) * mm});
            skLineSegment(sketch, "E86.MirrorCS", {"start": v(-144.58, 105.5) * mm, "end": v(-72.58, 105.5) * mm});
            skLineSegment(sketch, "E87.MirrorCS", {"start": v(-72.58, 105.5) * mm, "end": v(-72.58, 110.5) * mm});
            skLineSegment(sketch, "E88", {"start": v(128.47, 151) * mm, "end": v(-144.58, 151) * mm, "construction": true});
            skPoint(sketch, "E89", {"position": v(-72.58, 151) * mm});
            skPoint(sketch, "E90", {"position": v(-8.05, 151) * mm});
            skSolve(sketch);
        }
        {
            var Q0;
            Q0 = qSketchRegion(id + "F33", true);
            extrude(context, id + "F34", {"entities" : qUnion([Q0]), "depth" : 31.75 * mm});
        }
        {
            var Q0;
            Q0=makeQuery(id+"F20.opExtrude","SWEPT_FACE",FACE,{"disambiguationData":[OSD([sQuery(id+"F19.wireOp",EDGE,"E59.right")])]});
            var sketch = newSketch(context, id + "F35", { "sketchPlane" : qUnion([Q0])});
            skLineSegment(sketch, "E91", {"start": v(368.3, 151) * mm, "end": v(311.55, 151) * mm});
            skSolve(sketch);
        }
        {
            var Q0;
            Q0=makeQuery(id+"F34.opExtrude","SWEPT_BODY",BODY,{"disambiguationData":[OSD([sQuery(id+"F33.wireOp",EDGE,"E78"),sQuery(id+"F33.wireOp",EDGE,"E79"),sQuery(id+"F33.wireOp",EDGE,"E80"),sQuery(id+"F33.wireOp",EDGE,"E81"),sQuery(id+"F33.wireOp",EDGE,"E82"),sQuery(id+"F33.wireOp",EDGE,"E84.MirrorCS"),sQuery(id+"F33.wireOp",EDGE,"E85.MirrorCS"),sQuery(id+"F33.wireOp",EDGE,"E86.MirrorCS"),sQuery(id+"F33.wireOp",EDGE,"E87.MirrorCS")])]});
            var Q1;
            Q1=sQuery(id+"F35.wireOp",EDGE,"E91");
            circularPattern(context, id + "F36", {"entities" : qUnion([Q0]), "axis" : qUnion([Q1]), "angle" : 180 * degree, "instanceCount" : 2});
        }
        {
            var Q0;
            Q0=makeQuery(id+"F20.opExtrude","CAP_FACE",FACE,{"disambiguationData":[OSD([sQuery(id+"F19.wireOp",EDGE,"E59.bottom"),sQuery(id+"F19.wireOp",EDGE,"E59.top"),sQuery(id+"F19.wireOp",EDGE,"E59.left"),sQuery(id+"F19.wireOp",EDGE,"E59.right")])],"isStart":true});
            var sketch = newSketch(context, id + "F37", { "sketchPlane" : qUnion([Q0])});
            skLineSegment(sketch, "E92.bottom", {"start": v(144.58, 180.05) * mm, "end": v(125.53, 180.05) * mm});
            skLineSegment(sketch, "E92.top", {"start": v(144.58, 161) * mm, "end": v(125.53, 161) * mm});
            skLineSegment(sketch, "E92.left", {"start": v(144.58, 180.05) * mm, "end": v(144.58, 161) * mm});
            skLineSegment(sketch, "E92.right", {"start": v(125.53, 180.05) * mm, "end": v(125.53, 161) * mm});
            skLineSegment(sketch, "E93.bottom", {"start": v(144.58, 117.65) * mm, "end": v(125.53, 117.65) * mm});
            skLineSegment(sketch, "E93.top", {"start": v(144.58, 136.7) * mm, "end": v(125.53, 136.7) * mm});
            skLineSegment(sketch, "E93.left", {"start": v(144.58, 117.65) * mm, "end": v(144.58, 136.7) * mm});
            skLineSegment(sketch, "E93.right", {"start": v(125.53, 117.65) * mm, "end": v(125.53, 136.7) * mm});
            skLineSegment(sketch, "E94", {"start": v(135.05, 161) * mm, "end": v(135.05, 136.7) * mm, "construction": true});
            skLineSegment(sketch, "E95", {"start": v(135.05, 148.85) * mm, "end": v(144.58, 148.85) * mm, "construction": true});
            skLineSegment(sketch, "E96", {"start": v(135.05, 180.05) * mm, "end": v(135.05, 204.35) * mm, "construction": true});
            skPoint(sketch, "E97", {"position": v(135.05, 192.2) * mm});
            skSolve(sketch);
        }
        {
            var Q0;
            Q0 = qSketchRegion(id + "F37", true);
            extrude(context, id + "F38", {"entities" : qUnion([Q0]), "operationType" : NewBodyOperationType.REMOVE, "oppositeDirection" : true, "depth" : 25.4 * mm});
        }
        {
            var Q0;
            Q0=makeQuery(id+"F16.opExtrude","SWEPT_FACE",FACE,{"disambiguationData":[OSD([sQuery(id+"F15.wireOp",EDGE,"E55.right")])]});
            var sketch = newSketch(context, id + "F39", { "sketchPlane" : qUnion([Q0])});
            skLineSegment(sketch, "E98.bottom", {"start": v(5.5, 235.8) * mm, "end": v(310.3, 235.8) * mm});
            skLineSegment(sketch, "E98.top", {"start": v(5.5, 223.1) * mm, "end": v(310.3, 223.1) * mm});
            skLineSegment(sketch, "E98.left", {"start": v(5.5, 235.8) * mm, "end": v(5.5, 223.1) * mm});
            skLineSegment(sketch, "E98.right", {"start": v(310.3, 235.8) * mm, "end": v(310.3, 223.1) * mm});
            skLineSegment(sketch, "E99.bottom", {"start": v(21.37, 223.1) * mm, "end": v(326.18, 223.1) * mm});
            skLineSegment(sketch, "E99.top", {"start": v(21.37, 210.4) * mm, "end": v(326.18, 210.4) * mm});
            skLineSegment(sketch, "E99.left", {"start": v(21.37, 223.1) * mm, "end": v(21.37, 210.4) * mm});
            skLineSegment(sketch, "E99.right", {"start": v(326.18, 223.1) * mm, "end": v(326.18, 210.4) * mm});
            skSolve(sketch);
        }
        {
            var Q0;
            Q0=makeQuery(id+"F39.imprint","IMPRINT",FACE,{"disambiguationData":[TD([[makeQuery(id+"F39.imprint","IMPRINT",EDGE,{"derivedFrom":sQuery(id+"F39.wireOp",EDGE,"E98.bottom")}),1.0]])]});
            extrude(context, id + "F40", {"entities" : qUnion([Q0]), "depth" : 44.45 * mm});
        }
        {
            var Q0;
            {var subQ0=sQuery(id+"F39.wireOp",EDGE,"E99.top");Q0=makeQuery(id+"F39.imprint","IMPRINT",FACE,{"disambiguationData":[TD([[makeQuery(id+"F39.imprint","IMPRINT",EDGE,{"derivedFrom":subQ0}),1.0]])]});}
            var Q1;
            {var subQ1=sQuery(id+"F39.wireOp",EDGE,"E99.bottom");var subQ8=makeQuery(id+"F39.imprint","INTERSECT",VERTEX,{"derivedFrom":[sQuery(id+"F39.wireOp",EDGE,"E98.right"),subQ1]});Q1=makeQuery(id+"F39.imprint","IMPRINT",FACE,{"disambiguationData":[TD([[makeQuery(id+"F39.imprint","IMPRINT",EDGE,{"disambiguationData":[TD([[subQ8,-1.0]])],"derivedFrom":subQ1}),-1.0]])]});}
            extrude(context, id + "F41", {"entities" : qUnion([Q0, Q1]), "depth" : 44.45 * mm});
        }
        {
            var Q0;
            Q0=makeQuery(id+"F3.opExtrude","SWEPT_BODY",BODY,{"disambiguationData":[OSD([sQuery(id+"F2.wireOp",EDGE,"E40.bottom"),sQuery(id+"F2.wireOp",EDGE,"E40.top"),sQuery(id+"F2.wireOp",EDGE,"E40.left"),sQuery(id+"F2.wireOp",EDGE,"E40.right")])]});
            var Q1;
            Q1=makeQuery(id+"F24.opExtrude","SWEPT_BODY",BODY,{"disambiguationData":[OSD([sQuery(id+"F23.wireOp",EDGE,"E61.bottom"),sQuery(id+"F23.wireOp",EDGE,"E61.top"),sQuery(id+"F23.wireOp",EDGE,"E61.left"),sQuery(id+"F23.wireOp",EDGE,"E61.right")])]});
            var Q2;
            Q2=makeQuery(id+"F30.opExtrude","SWEPT_BODY",BODY,{"disambiguationData":[OSD([sQuery(id+"F29.wireOp",EDGE,"E68.bottom"),sQuery(id+"F29.wireOp",EDGE,"E68.top"),sQuery(id+"F29.wireOp",EDGE,"E68.left"),sQuery(id+"F29.wireOp",EDGE,"E68.right")])]});
            var Q3;
            Q3=makeQuery(id+"F26.opExtrude","SWEPT_BODY",BODY,{"disambiguationData":[OSD([sQuery(id+"F25.wireOp",EDGE,"E62.bottom"),sQuery(id+"F25.wireOp",EDGE,"E62.top"),sQuery(id+"F25.wireOp",EDGE,"E62.left"),sQuery(id+"F25.wireOp",EDGE,"E62.right")])]});
            var Q4;
            Q4=makeQuery(id+"F20.opExtrude","SWEPT_BODY",BODY,{"disambiguationData":[OSD([sQuery(id+"F19.wireOp",EDGE,"E59.bottom"),sQuery(id+"F19.wireOp",EDGE,"E59.top"),sQuery(id+"F19.wireOp",EDGE,"E59.left"),sQuery(id+"F19.wireOp",EDGE,"E59.right")])]});
            var Q5;
            Q5=makeQuery(id+"F14.opExtrude","SWEPT_BODY",BODY,{"disambiguationData":[OSD([sQuery(id+"F13.wireOp",EDGE,"E54.bottom"),sQuery(id+"F13.wireOp",EDGE,"E54.top"),sQuery(id+"F13.wireOp",EDGE,"E54.left"),sQuery(id+"F13.wireOp",EDGE,"E54.right")])]});
            var Q6;
            Q6=makeQuery(id+"F1.opExtrude","SWEPT_BODY",BODY,{"disambiguationData":[OSD([sQuery(id+"F0.wireOp",EDGE,"E16"),sQuery(id+"F0.wireOp",EDGE,"E17"),sQuery(id+"F0.wireOp",EDGE,"E18"),sQuery(id+"F0.wireOp",EDGE,"E19"),sQuery(id+"F0.wireOp",EDGE,"E21.bottom")])]});
            var Q7;
            Q7=makeQuery(id+"F16.opExtrude","SWEPT_BODY",BODY,{"disambiguationData":[OSD([sQuery(id+"F15.wireOp",EDGE,"E55.bottom"),sQuery(id+"F15.wireOp",EDGE,"E55.top"),sQuery(id+"F15.wireOp",EDGE,"E55.left"),sQuery(id+"F15.wireOp",EDGE,"E55.right")])]});
            var Q8;
            Q8=makeQuery(id+"F1.opExtrude","SWEPT_BODY",BODY,{"disambiguationData":[OSD([sQuery(id+"F0.wireOp",EDGE,"E20.bottom"),sQuery(id+"F0.wireOp",EDGE,"E20.top"),sQuery(id+"F0.wireOp",EDGE,"E20.left"),sQuery(id+"F0.wireOp",EDGE,"E20.right")])]});
            var Q9;
            Q9=makeQuery(id+"F10.opExtrude","SWEPT_BODY",BODY,{"disambiguationData":[OSD([sQuery(id+"F9.wireOp",EDGE,"E48.bottom"),sQuery(id+"F9.wireOp",EDGE,"E48.top"),sQuery(id+"F9.wireOp",EDGE,"E48.left"),sQuery(id+"F9.wireOp",EDGE,"E48.right")])]});
            var Q10;
            Q10=makeQuery(id+"F18.opExtrude","SWEPT_BODY",BODY,{"disambiguationData":[OSD([sQuery(id+"F17.wireOp",EDGE,"E56.bottom"),sQuery(id+"F17.wireOp",EDGE,"E56.top"),sQuery(id+"F17.wireOp",EDGE,"E56.left"),sQuery(id+"F17.wireOp",EDGE,"E56.right"),sQuery(id+"F17.wireOp",EDGE,"E57.top"),sQuery(id+"F17.wireOp",EDGE,"E57.left")])]});
            var Q11;
            Q11=makeQuery(id+"F5.opExtrude","SWEPT_BODY",BODY,{"disambiguationData":[OSD([sQuery(id+"F4.wireOp",EDGE,"E41.bottom"),sQuery(id+"F4.wireOp",EDGE,"E41.top"),sQuery(id+"F4.wireOp",EDGE,"E41.left"),sQuery(id+"F4.wireOp",EDGE,"E41.right")])]});
            var Q12;
            Q12=makeQuery(id+"F1.opExtrude","SWEPT_BODY",BODY,{"disambiguationData":[OSD([sQuery(id+"F0.wireOp",EDGE,"E0.bottom"),sQuery(id+"F0.wireOp",EDGE,"E0.top"),sQuery(id+"F0.wireOp",EDGE,"E0.left"),sQuery(id+"F0.wireOp",EDGE,"E0.right")])]});
            var Q13;
            Q13=makeQuery(id+"F41.opExtrude","SWEPT_BODY",BODY,{"disambiguationData":[OSD([sQuery(id+"F39.wireOp",EDGE,"E99.bottom"),sQuery(id+"F39.wireOp",EDGE,"E99.top"),sQuery(id+"F39.wireOp",EDGE,"E99.left"),sQuery(id+"F39.wireOp",EDGE,"E99.right")])]});
            var Q14;
            Q14=makeQuery(id+"F40.opExtrude","SWEPT_BODY",BODY,{"disambiguationData":[OSD([sQuery(id+"F39.wireOp",EDGE,"E98.bottom"),sQuery(id+"F39.wireOp",EDGE,"E98.top"),sQuery(id+"F39.wireOp",EDGE,"E98.left"),sQuery(id+"F39.wireOp",EDGE,"E98.right"),sQuery(id+"F39.wireOp",EDGE,"E99.bottom")])]});
            var Q15;
            Q15=qCreatedBy(makeId("Right.planeOp"),FACE);
            mirror(context, id + "F42", {"entities" : qUnion([Q0, Q1, Q2, Q3, Q4, Q5, Q6, Q7, Q8, Q9, Q10, Q11, Q12, Q13, Q14]), "mirrorPlane" : qUnion([Q15])});
        }
        {
            var Q0;
            Q0=makeQuery(id+"F3.opExtrude","SWEPT_BODY",BODY,{"disambiguationData":[OSD([sQuery(id+"F2.wireOp",EDGE,"E40.bottom"),sQuery(id+"F2.wireOp",EDGE,"E40.top"),sQuery(id+"F2.wireOp",EDGE,"E40.left"),sQuery(id+"F2.wireOp",EDGE,"E40.right")])]});
            var Q1;
            Q1=makeQuery(id+"F42.opPattern","COPY",BODY,{"derivedFrom":makeQuery(id+"F3.opExtrude","SWEPT_BODY",BODY,{"disambiguationData":[OSD([sQuery(id+"F2.wireOp",EDGE,"E40.bottom"),sQuery(id+"F2.wireOp",EDGE,"E40.top"),sQuery(id+"F2.wireOp",EDGE,"E40.left"),sQuery(id+"F2.wireOp",EDGE,"E40.right")])]}),"instanceName":"1"});
            booleanBodies(context, id + "F43", {"operationType" : BooleanOperationType.UNION, "tools" : qUnion([Q0, Q1])});
        }
        {
            var Q0;
            {var subQ0=sQuery(id+"F2.wireOp",EDGE,"E40.top");var subQ1=sQuery(id+"F2.wireOp",EDGE,"E40.left");var subQ2=makeQuery(id+"F7.boolean.opBoolean","SPLIT",FACE,{"disambiguationData":[TD([makeQuery(id+"F3.opExtrude","SWEPT_FACE",FACE,{"disambiguationData":[OSD([subQ1])]})])],"derivedFrom":makeQuery(id+"F3.opExtrude","CAP_FACE",FACE,{"disambiguationData":[OSD([sQuery(id+"F2.wireOp",EDGE,"E40.bottom"),subQ0,subQ1,sQuery(id+"F2.wireOp",EDGE,"E40.right")])],"isStart":false})});Q0=makeQuery(id+"F43.opBoolean","MERGE",FACE,{"derivedFrom":[subQ2,makeQuery(id+"F42.opPattern","COPY",FACE,{"derivedFrom":subQ2,"instanceName":"1"})]});}
            var sketch = newSketch(context, id + "F44", { "sketchPlane" : qUnion([Q0])});
            skLineSegment(sketch, "E100.bottom", {"start": v(-20.12, 147.66) * mm, "end": v(-144.58, 147.66) * mm});
            skLineSegment(sketch, "E100.top", {"start": v(-20.12, 114.64) * mm, "end": v(-144.58, 114.64) * mm});
            skLineSegment(sketch, "E100.left", {"start": v(-20.12, 147.66) * mm, "end": v(-20.12, 114.64) * mm});
            skLineSegment(sketch, "E100.right", {"start": v(-144.58, 147.66) * mm, "end": v(-144.58, 114.64) * mm});
            skSolve(sketch);
        }
        {
            var Q0;
            Q0=makeQuery(id+"F44.imprint","IMPRINT",FACE,{"disambiguationData":[TD([[makeQuery(id+"F44.imprint","IMPRINT",EDGE,{"derivedFrom":sQuery(id+"F44.wireOp",EDGE,"E100.bottom")}),1.0]])]});
            extrude(context, id + "F45", {"entities" : qUnion([Q0]), "operationType" : NewBodyOperationType.REMOVE, "oppositeDirection" : true, "depth" : 25.4 * mm});
        }
        {
            var Q0;
            {var subQ0=makeQuery(id+"F3.opExtrude","CAP_FACE",FACE,{"disambiguationData":[OSD([sQuery(id+"F2.wireOp",EDGE,"E40.bottom"),sQuery(id+"F2.wireOp",EDGE,"E40.top"),sQuery(id+"F2.wireOp",EDGE,"E40.left"),sQuery(id+"F2.wireOp",EDGE,"E40.right")])],"isStart":true});Q0=makeQuery(id+"F43.opBoolean","MERGE",FACE,{"derivedFrom":[subQ0,makeQuery(id+"F42.opPattern","COPY",FACE,{"derivedFrom":subQ0,"instanceName":"1"})]});}
            var sketch = newSketch(context, id + "F46", { "sketchPlane" : qUnion([Q0])});
            skLineSegment(sketch, "E101.bottom", {"start": v(17.58, 112.23) * mm, "end": v(147.12, 112.23) * mm});
            skLineSegment(sketch, "E101.top", {"start": v(17.58, 150.08) * mm, "end": v(147.12, 150.08) * mm});
            skLineSegment(sketch, "E101.left", {"start": v(17.58, 112.23) * mm, "end": v(17.58, 150.08) * mm});
            skLineSegment(sketch, "E101.right", {"start": v(147.12, 112.23) * mm, "end": v(147.12, 150.08) * mm});
            skPoint(sketch, "E101.middle", {"position": v(82.35, 131.15) * mm});
            skPoint(sketch, "E101.middle.positionSnap0", {"position": v(144.58, 131.15) * mm});
            skPoint(sketch, "E101.middle.positionSnap1", {"position": v(82.35, 147.66) * mm});
            skPoint(sketch, "E101.centerSnap0", {"position": v(144.58, 131.15) * mm});
            skPoint(sketch, "E101.centerSnap1", {"position": v(82.35, 147.66) * mm});
            skSolve(sketch);
        }
        {
            var Q0;
            Q0 = qSketchRegion(id + "F46", true);
            extrude(context, id + "F47", {"entities" : qUnion([Q0]), "depth" : 3 * mm});
        }
        {
            var Q0;
            Q0 = qSketchRegion(id + "F44", true);
            var Q1;
            Q1=makeQuery(id+"F47.opExtrude","SWEPT_BODY",BODY,{"disambiguationData":[OSD([sQuery(id+"F46.wireOp",EDGE,"E101.bottom"),sQuery(id+"F46.wireOp",EDGE,"E101.top"),sQuery(id+"F46.wireOp",EDGE,"E101.left"),sQuery(id+"F46.wireOp",EDGE,"E101.right")])]});
            extrude(context, id + "F48", {"entities" : qUnion([Q0]), "operationType" : NewBodyOperationType.ADD, "depth" : 151.64 * mm, "hasSecondDirection" : true, "secondDirectionBound" : SecondDirectionBoundingType.UP_TO_BODY, "secondDirectionOppositeDirection" : true, "secondDirectionBoundEntityBody" : qUnion([Q1]), "secondDirectionDepth" : 25.4 * mm});
        }
    });
